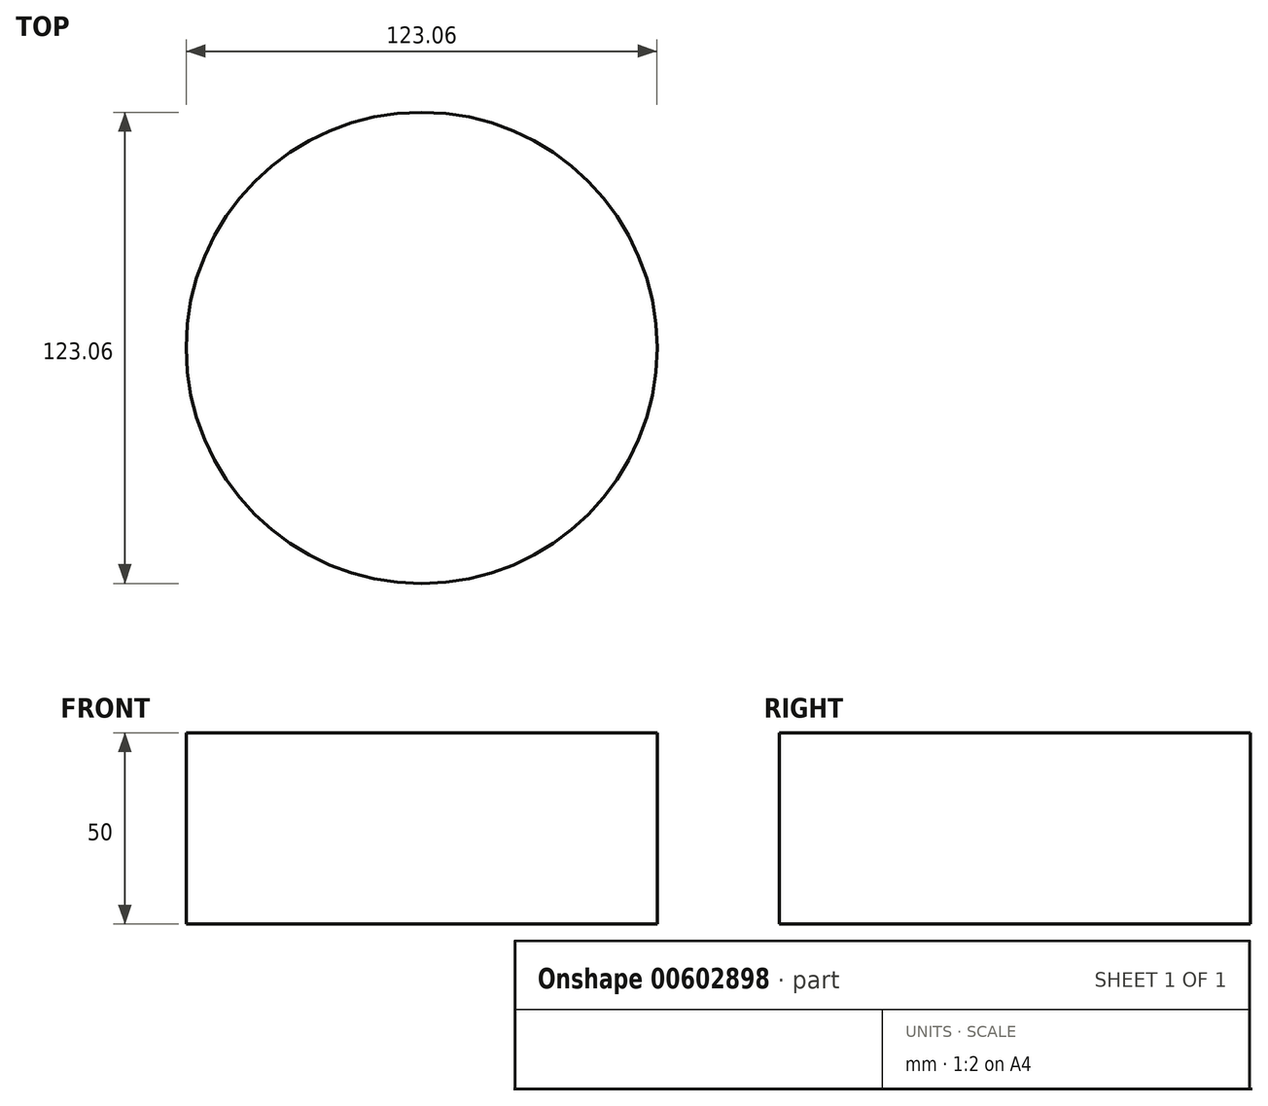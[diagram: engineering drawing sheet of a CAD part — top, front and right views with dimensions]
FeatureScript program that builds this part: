
annotation { "Feature Type Name" : "Feature", "Feature Type Description" : "" }
export const myFeature = defineFeature(function(context is Context, id is Id, definition is map)
    precondition{}
    {
        {
            var Q0;
            Q0=qCreatedBy(makeId("Top.planeOp"),FACE);
            var sketch = newSketch(context, id + "F0", { "sketchPlane" : qUnion([Q0])});
            skCircle(sketch, "E0", {"center": v(0, 0) * mm, "radius": 61.53 * mm});
            skSolve(sketch);
        }
        {
            var Q0;
            Q0 = qSketchRegion(id + "F0", true);
            extrude(context, id + "F1", {"entities" : qUnion([Q0]), "depth" : 50 * mm, "offsetDistance" : 25 * mm});
        }
    });
